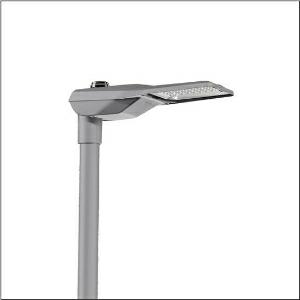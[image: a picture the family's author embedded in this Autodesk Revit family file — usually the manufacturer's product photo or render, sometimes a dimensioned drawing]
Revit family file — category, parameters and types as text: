
# Revit family: streetlight_sl_21_mini___stw1_0a_5xe6e37n08jb_6c36
name_source: partatom
category: Lighting Fixtures
units: mm (PartAtom-declared; Revit-internal decimal feet)

## family parameters
Cut with Voids When Loaded = No
Host = Face
Light Source = No
Part Type = Normal
Room Calculation Point = No
Round Connector Dimension = Use Diameter
Shared = No

## types (1)
- --- (1 x LED, 12830 lm, 87.3 W, 3000K)
    Apparent Load = 87 VA
    CIE Flux Codes = 39 75 98 100 100
    Color Rendering = 70
    Color Temperature = 3000K
    Default Elevation = 1800 mm
    Description = Streetlight SL 21 mini, mast luminaire, primary light control with lens, of PMMA, primary optical cover: cover, of toughened safety glass, transparent, light distribution: STW1.0a, light emission: direct distribution, primary light characteristic: asymmetric, installation type: side-entry, LED, 3G 2.5mm², High Power LED, rated luminous flux: 12.830lm, luminous efficacy: 147lm/W, light colour: 730, colour temperature: 3000K, control gear: NEMA (7pin), control: overheat protection, pre-setting: linear dimming characteristic, constant luminous flux control, time-dependent luminous flux control, flexible luminous flux parameterisation, mains connection: 230..240V, AC, 50/60Hz, connection cable pre-assembled, cable length: 10,5m, wiring characteristics: H05VV-F, start of lifetime: 87W, end of service life: 90W, reduction: 40W, luminaire housing, of diecast aluminium (EN AC-44300), powder-coated, SITECO metallic grey (DB 702S), corrosivity category C5 high according to DIN EN ISO 12944, multi-level sealing system, sealing non-destructively replaceable, inclination adjustable: 0°, 5°, 10°, 15°, length: 628mm, width: 235mm, height: 110mm, spigot size: 42mm (side-entry), mounting height: 4..8m, protection rating (complete): IP66, insulation class (complete): insulation class I (protective earthing), certification: CE, ENEC, ENEC+, VDE, impact resistance: IK10, permissible operating ambient temperature for outdoor applications: -40..+50°C, standard-compliant lighting for roads and squares, packaging unit: 1 piece

Light Distribution: STW1.0a
    Height = 110 mm
    Lamp = 1 x LED
    Lamp Light Flux = 12830 lm
    Lamp Power = 87.3 W
    Lamp count = 1
    Length = 625 mm
    Luminous efficacy = 147 lm/W
    Manufacturer = Siteco
    ModVariant = No
    Model = 5XE6E37N08JB
    Number of Poles = 1
    OnlyDefault = Yes
    Power Factor = 1
    Product Name = Streetlight SL 21 mini | STW1.0a
    Product group = mast luminaire | pylon top
    ProductGroupID = 6100
    Protection Class = Protection class I
    Protection Degree = IP 66
    RLX_Detail_Level = 1
    RLX_Emergency_Light_Flux = 0 lm
    RLX_Emergency_Type = 0
    RLX_Emergency_Type_DB = No
    RlxData = <blob elided: 26069 chars, md5=fa350c3a>
    Socket = socket
    Standby Power = 0 W
    System Light Flux = 12830 lm
    System Power = 87 W
    Type Comments = factory setting: luminous flux: 100 % | dim-lin: 254 | 915 mA
    Type Image = l_1294379.jpg
    URL = http://relux.com
    VarID = @adj_134507
    Voltage = 0 V
    Weight = 0.00 kg
    Width = 234 mm

## geometry (parser evidence)
native form markers: Blend x4, Sweep x13
no freeform markers — native parametric forms only
